# Revit family: DockEquipment_RainShelter_SuperSeal_0601
name_source: partatom
category: Generic Models
revit_build: Autodesk Revit Architecture 2012 (Build: 20110309_2315(x64)
units: mm (PartAtom-declared; Revit-internal decimal feet)

## types (1)
- DockEquipment_RainShelter_SuperSeal_0601
    Bumper Width = 0' - 4"
    Construction Details = http://arcat.com
    Default Elevation = 4' - 0"
    Description = Super Seal
    Expected Lifespan (Years) = 0
    Maintenance Schedule (Months) = 0
    Manufacturer = Super-Seal Mfg. Ltd
    Manufacturer Fax = 905-850-4440
    Manufacturer Website = http://www.supersealmfg.com
    Material = Plastic - Vinyl - Super Seal - Blue
    Model = As Specified
    Product Data = http://arcat.com
    Revision = R1_07-2011
    Sales Information = http://www.supersealmfg.com
    Send Message = http://www.arcat.com &mf=
    Slope Rise = 0' - 6"
    URL = http://www.supersealmfg.com
    Unit Depth = 4' - 0"
    Warranty Duration (Years) = 0

## geometry (parser evidence)
native form markers: Blend x24, Sweep x1
no freeform markers — native parametric forms only
